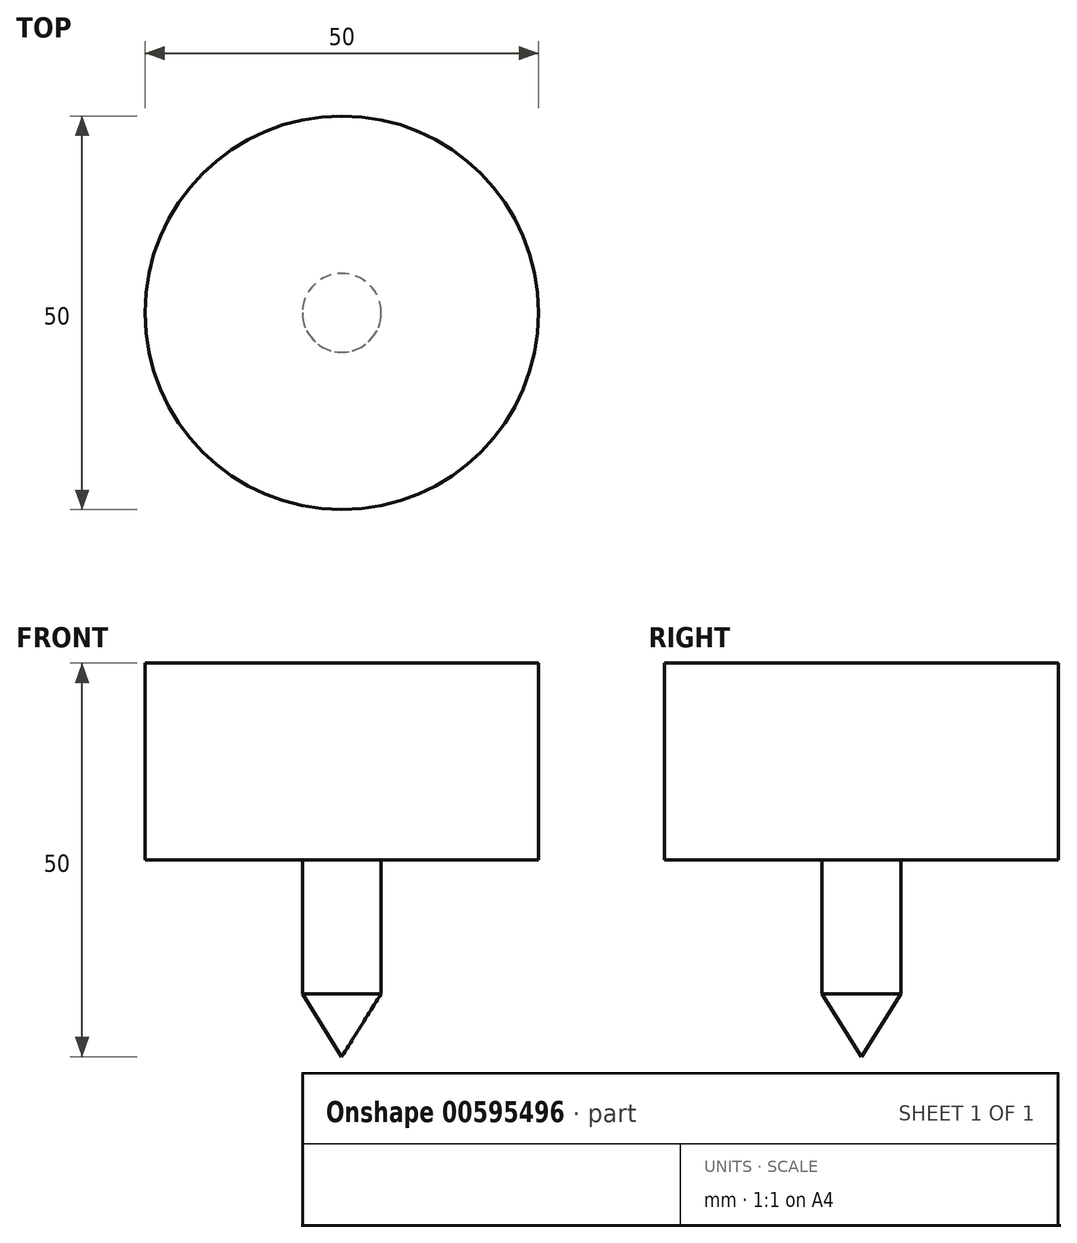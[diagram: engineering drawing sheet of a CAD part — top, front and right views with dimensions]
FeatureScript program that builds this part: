
annotation { "Feature Type Name" : "Feature", "Feature Type Description" : "" }
export const myFeature = defineFeature(function(context is Context, id is Id, definition is map)
    precondition{}
    {
        {
            var Q0;
            Q0=qCreatedBy(makeId("Front.planeOp"),FACE);
            var sketch = newSketch(context, id + "F0", { "sketchPlane" : qUnion([Q0])});
            skLineSegment(sketch, "E0", {"start": v(0, 0) * mm, "end": v(0, 50) * mm});
            skLineSegment(sketch, "E1", {"start": v(25, 50) * mm, "end": v(25, 25) * mm});
            skLineSegment(sketch, "E2", {"start": v(25, 25) * mm, "end": v(5, 25) * mm});
            skLineSegment(sketch, "E3", {"start": v(5, 25) * mm, "end": v(5, 8) * mm});
            skLineSegment(sketch, "E4", {"start": v(0, 50) * mm, "end": v(25, 50) * mm});
            skLineSegment(sketch, "E5", {"start": v(0, 0) * mm, "end": v(5, 8) * mm});
            skSolve(sketch);
        }
        {
            var Q0;
            Q0=makeQuery(id+"F0.imprint","IMPRINT",FACE,{"disambiguationData":[TD([[makeQuery(id+"F0.imprint","IMPRINT",EDGE,{"derivedFrom":sQuery(id+"F0.wireOp",EDGE,"E0")}),-1.0]])]});
            var Q1;
            Q1=sQuery(id+"F0.wireOp",EDGE,"E0");
            revolve(context, id + "F1", {"entities" : qUnion([Q0]), "axis" : qUnion([Q1]), "revolveType" : RevolveType.FULL});
        }
    });
